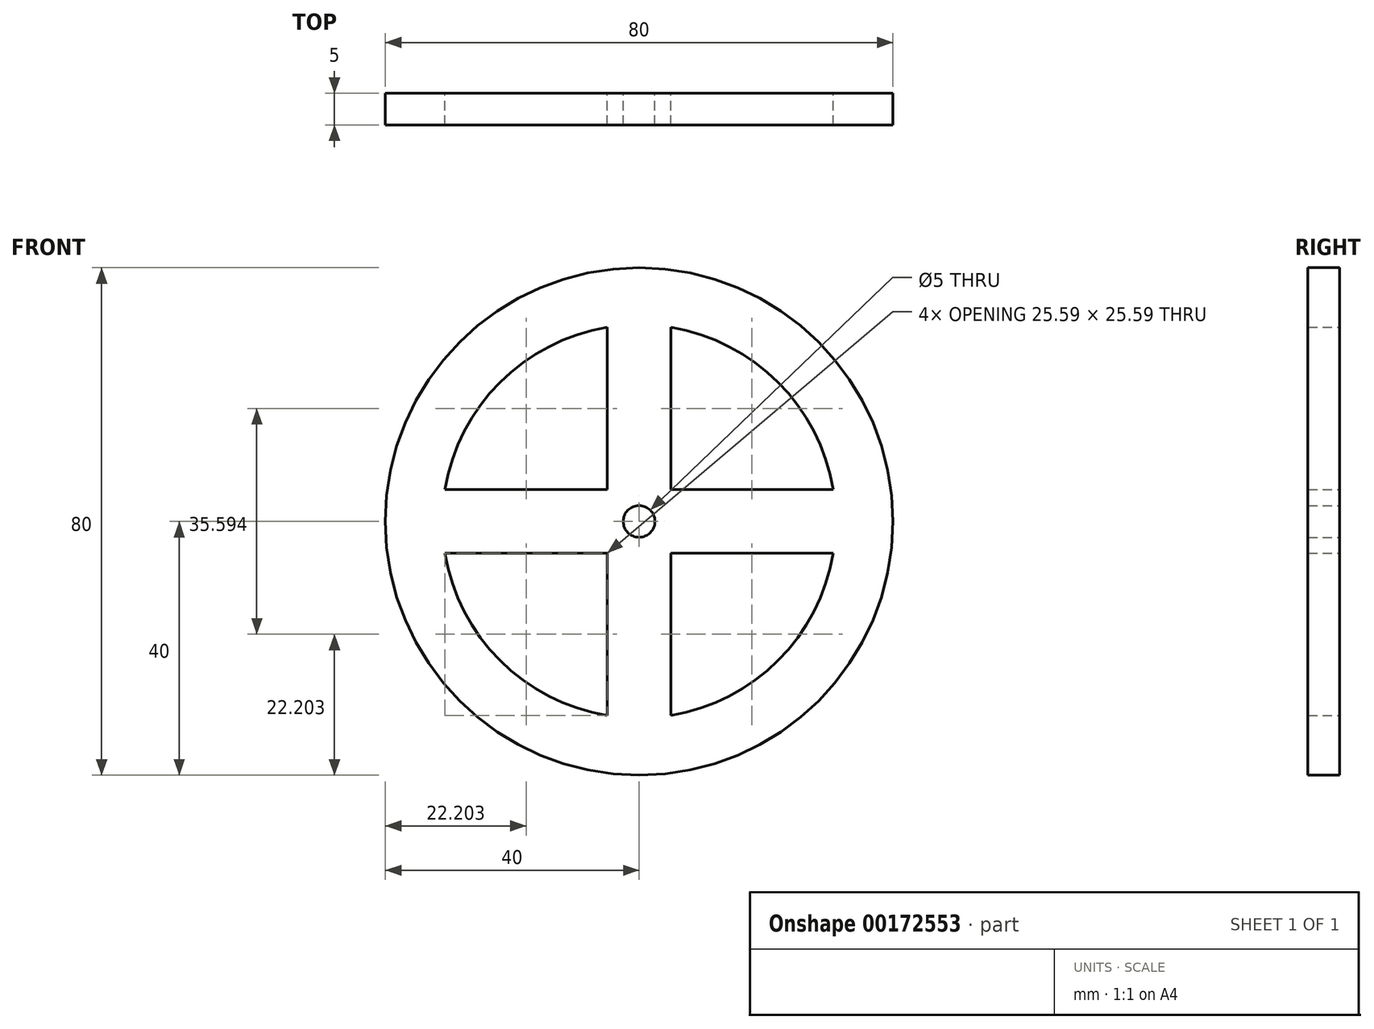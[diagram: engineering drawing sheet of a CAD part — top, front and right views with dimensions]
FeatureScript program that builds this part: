
annotation { "Feature Type Name" : "Feature", "Feature Type Description" : "" }
export const myFeature = defineFeature(function(context is Context, id is Id, definition is map)
    precondition{}
    {
        {
            var Q0;
            Q0=qCreatedBy(makeId("Front.planeOp"),FACE);
            var sketch = newSketch(context, id + "F0", { "sketchPlane" : qUnion([Q0])});
            skCircle(sketch, "E0", {"center": v(0, 0) * mm, "radius": 40 * mm});
            skArc(sketch, "E1", {"start": v(-5, 30.6) * mm, "mid": v(-21.92, 21.92) * mm, "end": v(-30.6, 5) * mm});
            skArc(sketch, "E2", {"start": v(-5.6, -5) * mm, "mid": v(-5.3, -5.3) * mm, "end": v(-5, -5.6) * mm});
            skCircle(sketch, "E3", {"center": v(0, 0) * mm, "radius": 2.5 * mm});
            skLineSegment(sketch, "E4", {"start": v(0, 0) * mm, "end": v(0, 31) * mm, "construction": true});
            skLineSegment(sketch, "E5", {"start": v(0, 0) * mm, "end": v(31, 0) * mm, "construction": true});
            skLineSegment(sketch, "E6", {"start": v(0, 0) * mm, "end": v(0, -31) * mm, "construction": true});
            skLineSegment(sketch, "E7", {"start": v(0, 0) * mm, "end": v(-4.34, 0) * mm});
            skLineSegment(sketch, "E8.0", {"start": v(-5, 5) * mm, "end": v(-5, 30.6) * mm});
            skLineSegment(sketch, "E9.0", {"start": v(5, 5) * mm, "end": v(5, 30.6) * mm});
            skLineSegment(sketch, "E10.0", {"start": v(-5, 5) * mm, "end": v(-30.6, 5) * mm});
            skLineSegment(sketch, "E11.0", {"start": v(-5, -5) * mm, "end": v(-30.6, -5) * mm});
            skLineSegment(sketch, "E12.0", {"start": v(-5, -5) * mm, "end": v(-5, -30.6) * mm});
            skLineSegment(sketch, "E13.0", {"start": v(5, -5) * mm, "end": v(5, -30.6) * mm});
            skLineSegment(sketch, "E14.0", {"start": v(5, 5) * mm, "end": v(30.6, 5) * mm});
            skLineSegment(sketch, "E15.0", {"start": v(5, -5) * mm, "end": v(30.6, -5) * mm});
            skLineSegment(sketch, "E16.trimOffspring", {"start": v(-5, 39.69) * mm, "end": v(-5, 40) * mm});
            skLineSegment(sketch, "E17.trimOffspring", {"start": v(5, 39.69) * mm, "end": v(5, 40) * mm});
            skLineSegment(sketch, "E18.trimOffspring", {"start": v(-39.69, 5) * mm, "end": v(-40, 5) * mm});
            skLineSegment(sketch, "E19.trimOffspring", {"start": v(-39.69, -5) * mm, "end": v(-40, -5) * mm});
            skLineSegment(sketch, "E20.trimOffspring", {"start": v(5, -39.69) * mm, "end": v(5, -40) * mm});
            skLineSegment(sketch, "E21.trimOffspring", {"start": v(-5, -39.69) * mm, "end": v(-5, -40) * mm});
            skLineSegment(sketch, "E22.trimOffspring", {"start": v(39.69, -5) * mm, "end": v(40, -5) * mm});
            skLineSegment(sketch, "E23.trimOffspring", {"start": v(39.69, 5) * mm, "end": v(40, 5) * mm});
            skArc(sketch, "E24.trimOffspring", {"start": v(-30.6, -5) * mm, "mid": v(-21.92, -21.92) * mm, "end": v(-5, -30.6) * mm});
            skArc(sketch, "E25.trimOffspring", {"start": v(5, -30.6) * mm, "mid": v(21.92, -21.92) * mm, "end": v(30.6, -5) * mm});
            skArc(sketch, "E26.trimOffspring", {"start": v(30.6, 5) * mm, "mid": v(21.92, 21.92) * mm, "end": v(5, 30.6) * mm});
            skLineSegment(sketch, "E27.trimOffspring", {"start": v(-5, 0) * mm, "end": v(-31, 0) * mm, "construction": true});
            skArc(sketch, "E28.trimOffspring", {"start": v(-5, 5.6) * mm, "mid": v(-5.3, 5.3) * mm, "end": v(-5.6, 5) * mm});
            skArc(sketch, "E29.trimOffspring", {"start": v(5.6, 5) * mm, "mid": v(5.3, 5.3) * mm, "end": v(5, 5.6) * mm});
            skArc(sketch, "E30.trimOffspring", {"start": v(5, -5.6) * mm, "mid": v(5.3, -5.3) * mm, "end": v(5.6, -5) * mm});
            skSolve(sketch);
        }
        {
            var Q0;
            Q0 = qSketchRegion(id + "F0", true);
            extrude(context, id + "F1", {"entities" : qUnion([Q0]), "endBound" : BoundingType.SYMMETRIC, "depth" : 5 * mm});
        }
    });
